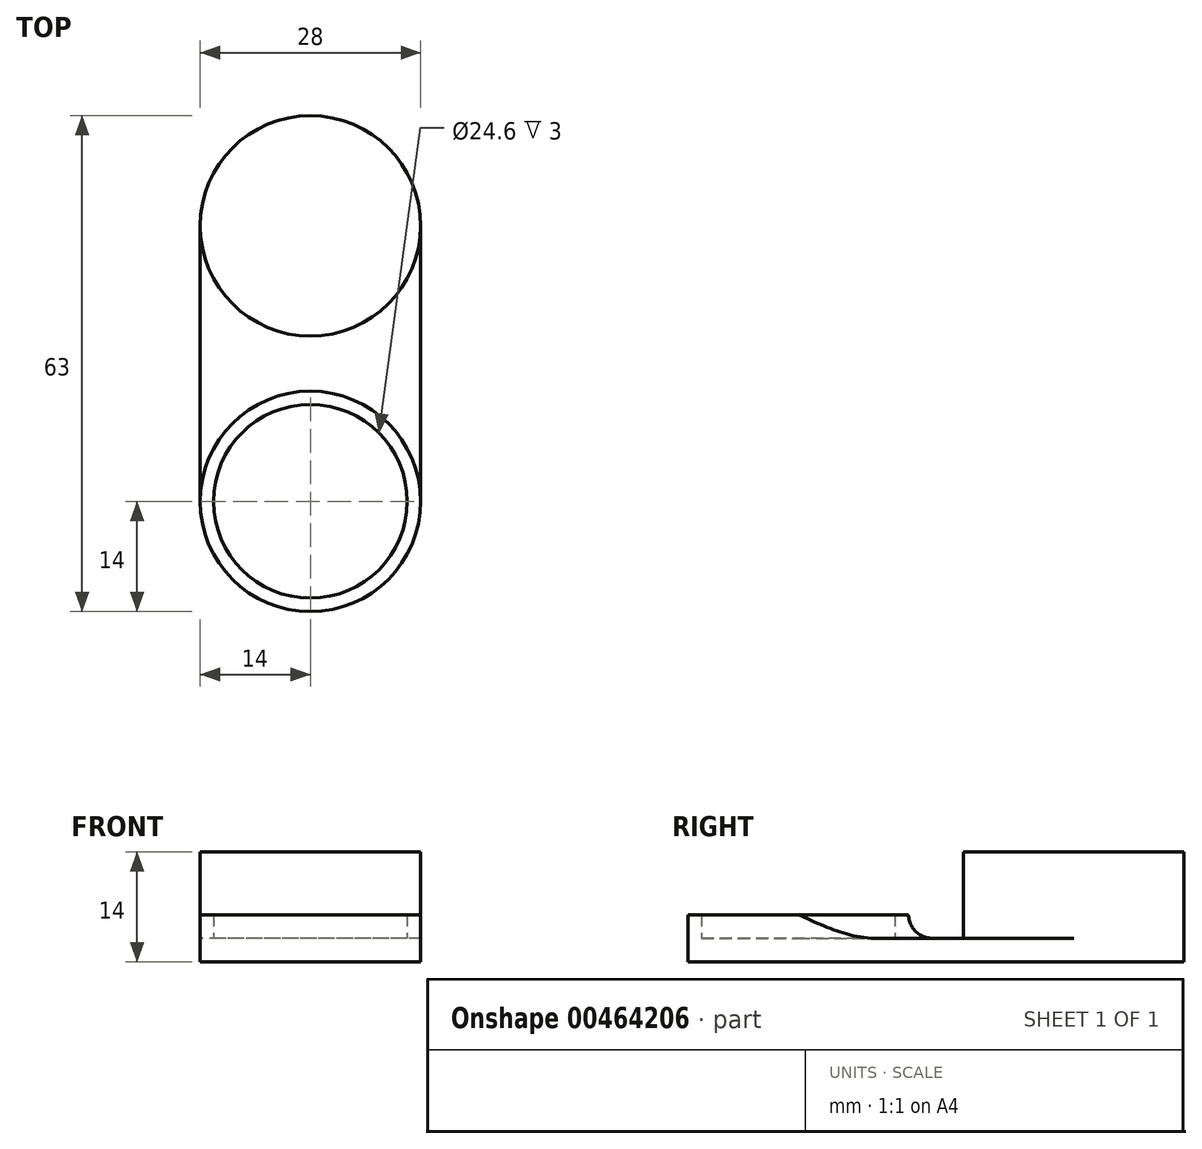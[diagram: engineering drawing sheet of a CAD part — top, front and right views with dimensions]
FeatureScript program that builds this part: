
annotation { "Feature Type Name" : "Feature", "Feature Type Description" : "" }
export const myFeature = defineFeature(function(context is Context, id is Id, definition is map)
    precondition{}
    {
        {
            var Q0;
            Q0=qCreatedBy(makeId("Top.planeOp"),FACE);
            var sketch = newSketch(context, id + "F0", { "sketchPlane" : qUnion([Q0])});
            skLineSegment(sketch, "E0", {"start": v(0, 0) * mm, "end": v(0, 17.5) * mm, "construction": true});
            skArc(sketch, "E1", {"start": v(14, 17.5) * mm, "mid": v(0, 31.5) * mm, "end": v(-14, 17.5) * mm});
            skLineSegment(sketch, "E2", {"start": v(0, 0) * mm, "end": v(20, 0) * mm, "construction": true});
            skArc(sketch, "E3.MirrorC", {"start": v(14, -17.5) * mm, "mid": v(0, -31.5) * mm, "end": v(-14, -17.5) * mm});
            skLineSegment(sketch, "E4", {"start": v(-14, 17.5) * mm, "end": v(-14, -17.5) * mm});
            skLineSegment(sketch, "E5", {"start": v(14, 17.5) * mm, "end": v(14, -17.5) * mm});
            skSolve(sketch);
        }
        {
            var Q0;
            Q0 = qSketchRegion(id + "F0", true);
            extrude(context, id + "F1", {"entities" : qUnion([Q0]), "depth" : 3 * mm});
        }
        {
            var Q0;
            Q0=makeQuery(id+"F1.opExtrude","CAP_FACE",FACE,{"disambiguationData":[OSD([sQuery(id+"F0.wireOp",EDGE,"E1"),sQuery(id+"F0.wireOp",EDGE,"E3.MirrorC"),sQuery(id+"F0.wireOp",EDGE,"E4"),sQuery(id+"F0.wireOp",EDGE,"E5")])],"isStart":false});
            var sketch = newSketch(context, id + "F2", { "sketchPlane" : qUnion([Q0])});
            skCircle(sketch, "E6", {"center": v(0, 17.5) * mm, "radius": 14 * mm});
            skSolve(sketch);
        }
        {
            var Q0;
            Q0 = qSketchRegion(id + "F2", true);
            extrude(context, id + "F3", {"entities" : qUnion([Q0]), "operationType" : NewBodyOperationType.ADD, "depth" : 11 * mm});
        }
        {
            var Q0;
            Q0=makeQuery(id+"F1.opExtrude","CAP_FACE",FACE,{"disambiguationData":[OSD([sQuery(id+"F0.wireOp",EDGE,"E1"),sQuery(id+"F0.wireOp",EDGE,"E3.MirrorC"),sQuery(id+"F0.wireOp",EDGE,"E4"),sQuery(id+"F0.wireOp",EDGE,"E5")])],"isStart":false});
            var sketch = newSketch(context, id + "F4", { "sketchPlane" : qUnion([Q0])});
            skCircle(sketch, "E7", {"center": v(0, -17.5) * mm, "radius": 14 * mm});
            skCircle(sketch, "E8", {"center": v(0, -17.5) * mm, "radius": 12.3 * mm});
            skSolve(sketch);
        }
        {
            var Q0;
            Q0 = qSketchRegion(id + "F4", true);
            extrude(context, id + "F5", {"entities" : qUnion([Q0]), "operationType" : NewBodyOperationType.ADD, "depth" : 3 * mm});
        }
        {
            var Q0;
            Q0=makeQuery(id+"F3.opExtrude","CAP_EDGE",EDGE,{"disambiguationData":[OSD([sQuery(id+"F2.wireOp",EDGE,"E6")])],"isStart":true});
            var Q1;
            Q1=makeQuery(id+"F5.opExtrude","CAP_EDGE",EDGE,{"disambiguationData":[OSD([sQuery(id+"F4.wireOp",EDGE,"E7")])],"isStart":true});
            fillet(context, id + "F6", {"entities" : qUnion([Q0, Q1]), "radius" : 3 * mm, "tangentPropagation" : true, "allowEdgeOverflow" : false});
        }
    });
